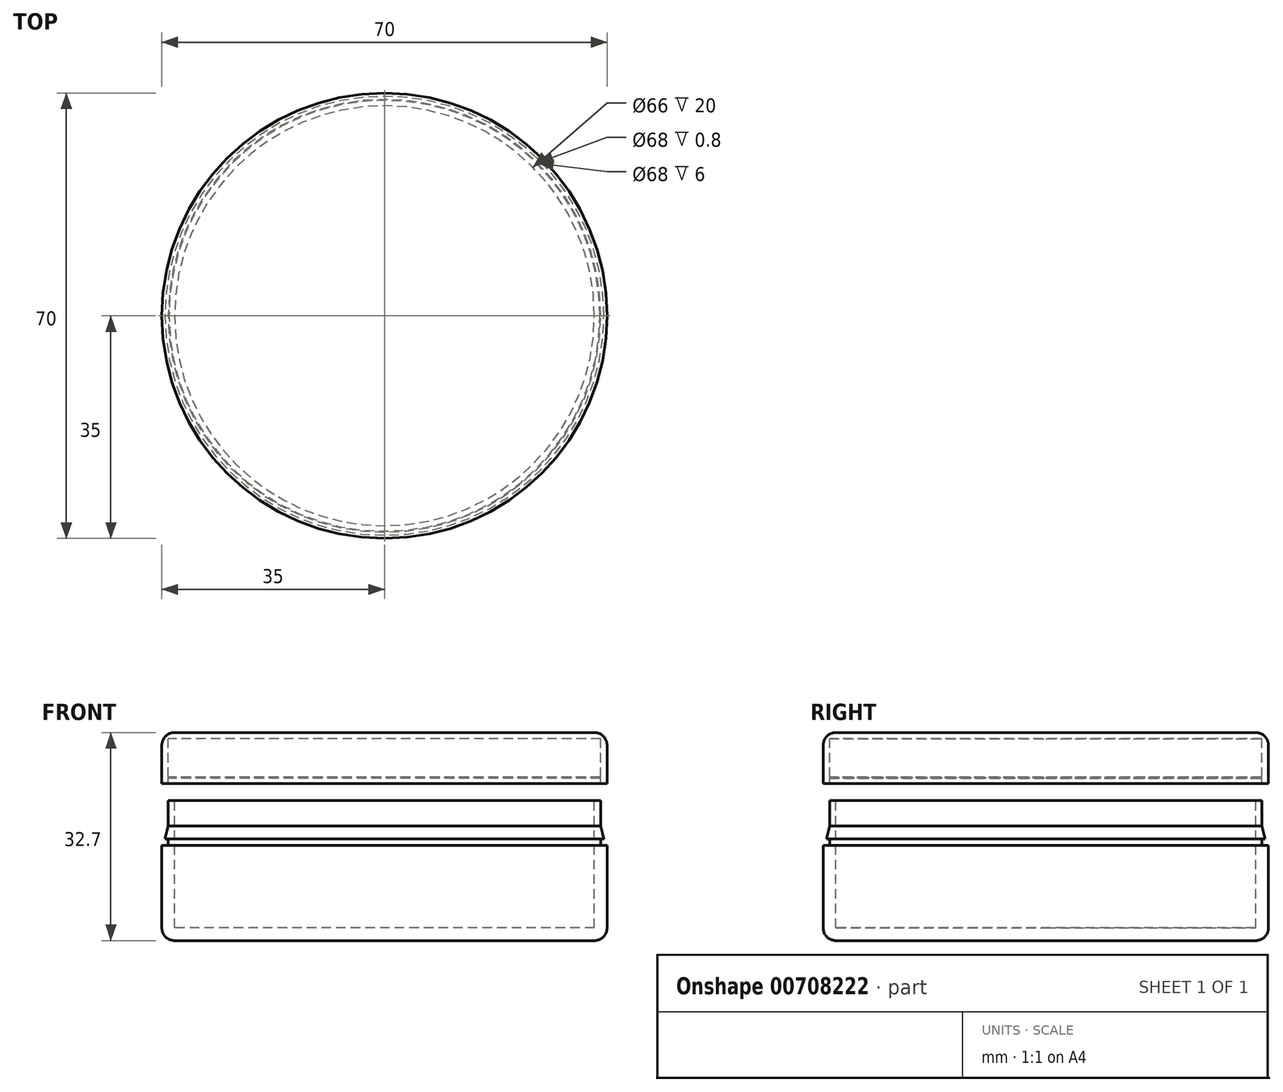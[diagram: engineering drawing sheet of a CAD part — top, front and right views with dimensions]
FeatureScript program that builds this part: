
annotation { "Feature Type Name" : "Feature", "Feature Type Description" : "" }
export const myFeature = defineFeature(function(context is Context, id is Id, definition is map)
    precondition{}
    {
        {
            var Q0;
            Q0=qCreatedBy(makeId("Front.planeOp"),FACE);
            var sketch = newSketch(context, id + "F0", { "sketchPlane" : qUnion([Q0])});
            skLineSegment(sketch, "E0", {"start": v(0, -0.07) * mm, "end": v(-35, -0.07) * mm});
            skLineSegment(sketch, "E1", {"start": v(-33, 21.93) * mm, "end": v(-33, 1.93) * mm});
            skLineSegment(sketch, "E2", {"start": v(-33, 1.93) * mm, "end": v(0, 1.93) * mm});
            skLineSegment(sketch, "E3", {"start": v(0, 1.93) * mm, "end": v(0, -0.07) * mm});
            skLineSegment(sketch, "E4", {"start": v(-35, 14.91) * mm, "end": v(-34, 14.91) * mm});
            skLineSegment(sketch, "E5", {"start": v(-35, 14.91) * mm, "end": v(-35, -0.07) * mm});
            skLineSegment(sketch, "E6", {"start": v(-34, 21.91) * mm, "end": v(-33, 21.93) * mm});
            skPoint(sketch, "E7", {"position": v(-34, 17.91) * mm});
            skPoint(sketch, "E8", {"position": v(-34, 15.91) * mm});
            skLineSegment(sketch, "E9", {"start": v(-34, 15.91) * mm, "end": v(-34.5, 15.91) * mm});
            skLineSegment(sketch, "E10", {"start": v(-34.5, 15.91) * mm, "end": v(-34, 17.91) * mm});
            skLineSegment(sketch, "E11", {"start": v(-34, 21.91) * mm, "end": v(-34, 17.91) * mm});
            skLineSegment(sketch, "E12", {"start": v(-34, 15.91) * mm, "end": v(-34, 14.91) * mm});
            skLineSegment(sketch, "E13", {"start": v(-35, 32.63) * mm, "end": v(0, 32.63) * mm});
            skLineSegment(sketch, "E14", {"start": v(-34, 31.63) * mm, "end": v(-34, 24.63) * mm});
            skLineSegment(sketch, "E15", {"start": v(-34, 24.63) * mm, "end": v(-35, 24.63) * mm});
            skLineSegment(sketch, "E16", {"start": v(-35, 24.63) * mm, "end": v(-35, 32.63) * mm});
            skLineSegment(sketch, "E17", {"start": v(-34, 31.63) * mm, "end": v(0, 31.63) * mm});
            skLineSegment(sketch, "E18", {"start": v(0, 31.63) * mm, "end": v(0, 32.63) * mm});
            skPoint(sketch, "E19", {"position": v(-34, 24.63) * mm});
            skPoint(sketch, "E20", {"position": v(-34, 25.43) * mm});
            skPoint(sketch, "E21", {"position": v(-34, 25.63) * mm});
            skLineSegment(sketch, "E22", {"start": v(-34, 25.43) * mm, "end": v(-33.87, 25.54) * mm});
            skLineSegment(sketch, "E23", {"start": v(-33.87, 25.54) * mm, "end": v(-34, 25.63) * mm});
            skSolve(sketch);
        }
        {
            var Q0;
            Q0 = qSketchRegion(id + "F0", true);
            var Q1;
            Q1=sQuery(id+"F0.wireOp",EDGE,"E3");
            revolve(context, id + "F1", {"surfaceOperationType" : NewSurfaceOperationType.NEW, "entities" : qUnion([Q0]), "axis" : qUnion([Q1]), "revolveType" : RevolveType.FULL});
        }
        {
            var Q0;
            Q0=makeQuery(id+"F1.opRevolve","SWEPT_EDGE",EDGE,{"disambiguationData":[OSD([sQuery(id+"F0.wireOp",EDGE,"E13"),sQuery(id+"F0.wireOp",EDGE,"E16")])]});
            var Q1;
            Q1=makeQuery(id+"F1.opRevolve","SWEPT_EDGE",EDGE,{"disambiguationData":[OSD([sQuery(id+"F0.wireOp",EDGE,"E0"),sQuery(id+"F0.wireOp",EDGE,"E5")])]});
            fillet(context, id + "F2", {"entities" : qUnion([Q0, Q1]), "radius" : 2 * mm, "tangentPropagation" : true, "allowEdgeOverflow" : false});
        }
    });
